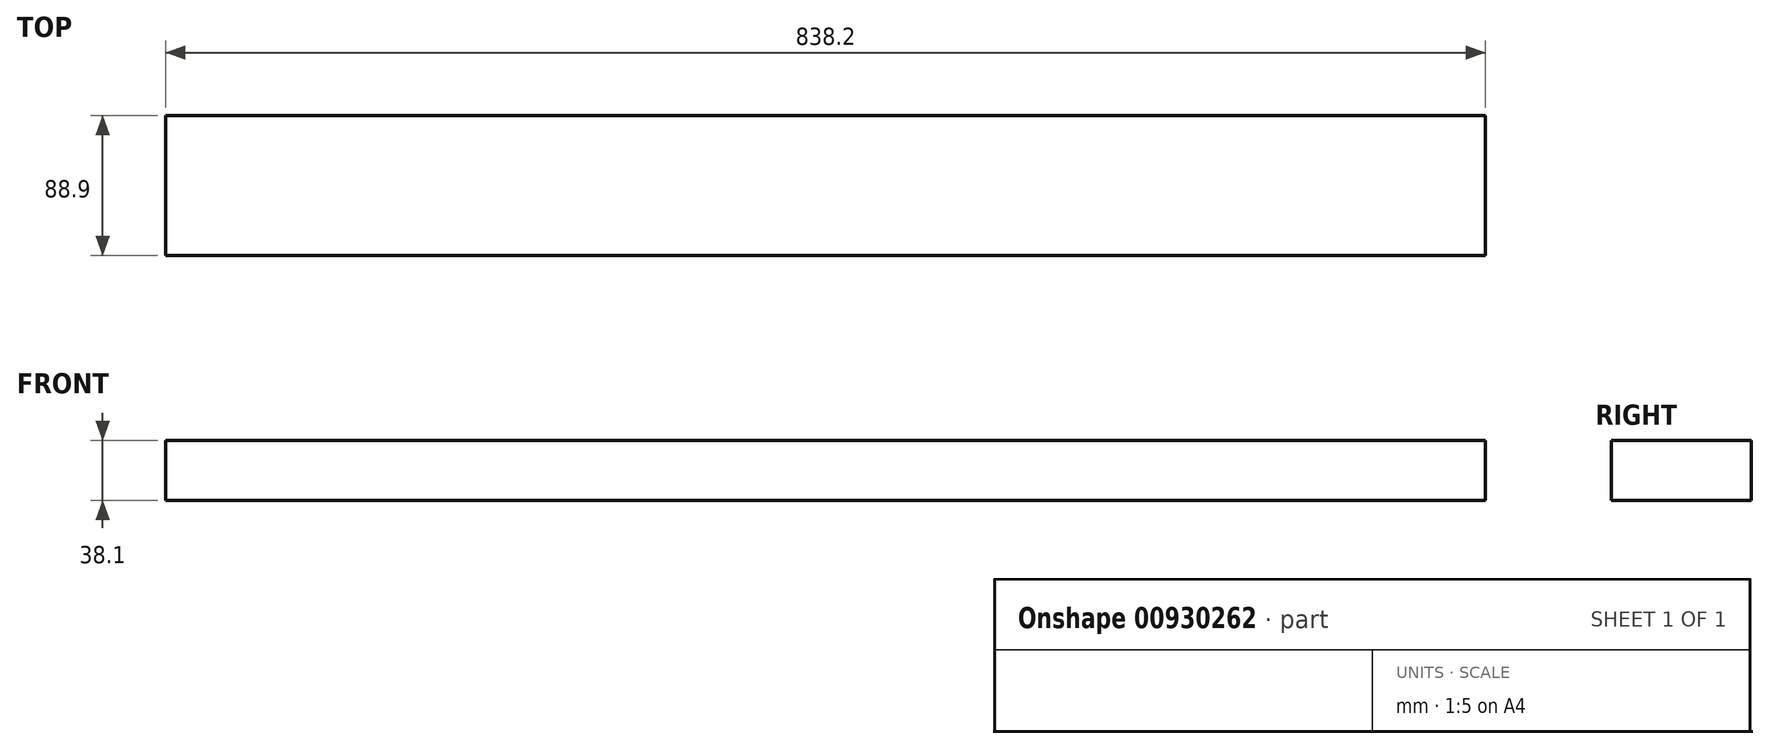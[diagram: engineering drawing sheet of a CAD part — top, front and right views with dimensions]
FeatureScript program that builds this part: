
annotation { "Feature Type Name" : "Feature", "Feature Type Description" : "" }
export const myFeature = defineFeature(function(context is Context, id is Id, definition is map)
    precondition{}
    {
        {
            var Q0;
            Q0=qCreatedBy(makeId("Right.planeOp"),FACE);
            var sketch = newSketch(context, id + "F0", { "sketchPlane" : qUnion([Q0])});
            skLineSegment(sketch, "E0.bottom", {"start": v(44.45, -19.05) * mm, "end": v(-44.45, -19.05) * mm});
            skLineSegment(sketch, "E0.top", {"start": v(44.45, 19.05) * mm, "end": v(-44.45, 19.05) * mm});
            skLineSegment(sketch, "E0.left", {"start": v(44.45, -19.05) * mm, "end": v(44.45, 19.05) * mm});
            skLineSegment(sketch, "E0.right", {"start": v(-44.45, -19.05) * mm, "end": v(-44.45, 19.05) * mm});
            skPoint(sketch, "E0.middle", {"position": v(0, 0) * mm});
            skSolve(sketch);
        }
        {
            var Q0;
            Q0=qSketchRegion(id+"F0",true);
            extrude(context, id + "F1", {"entities" : qUnion([Q0]), "endBound" : BoundingType.SYMMETRIC, "depth" : 838.2 * mm});
        }
    });
